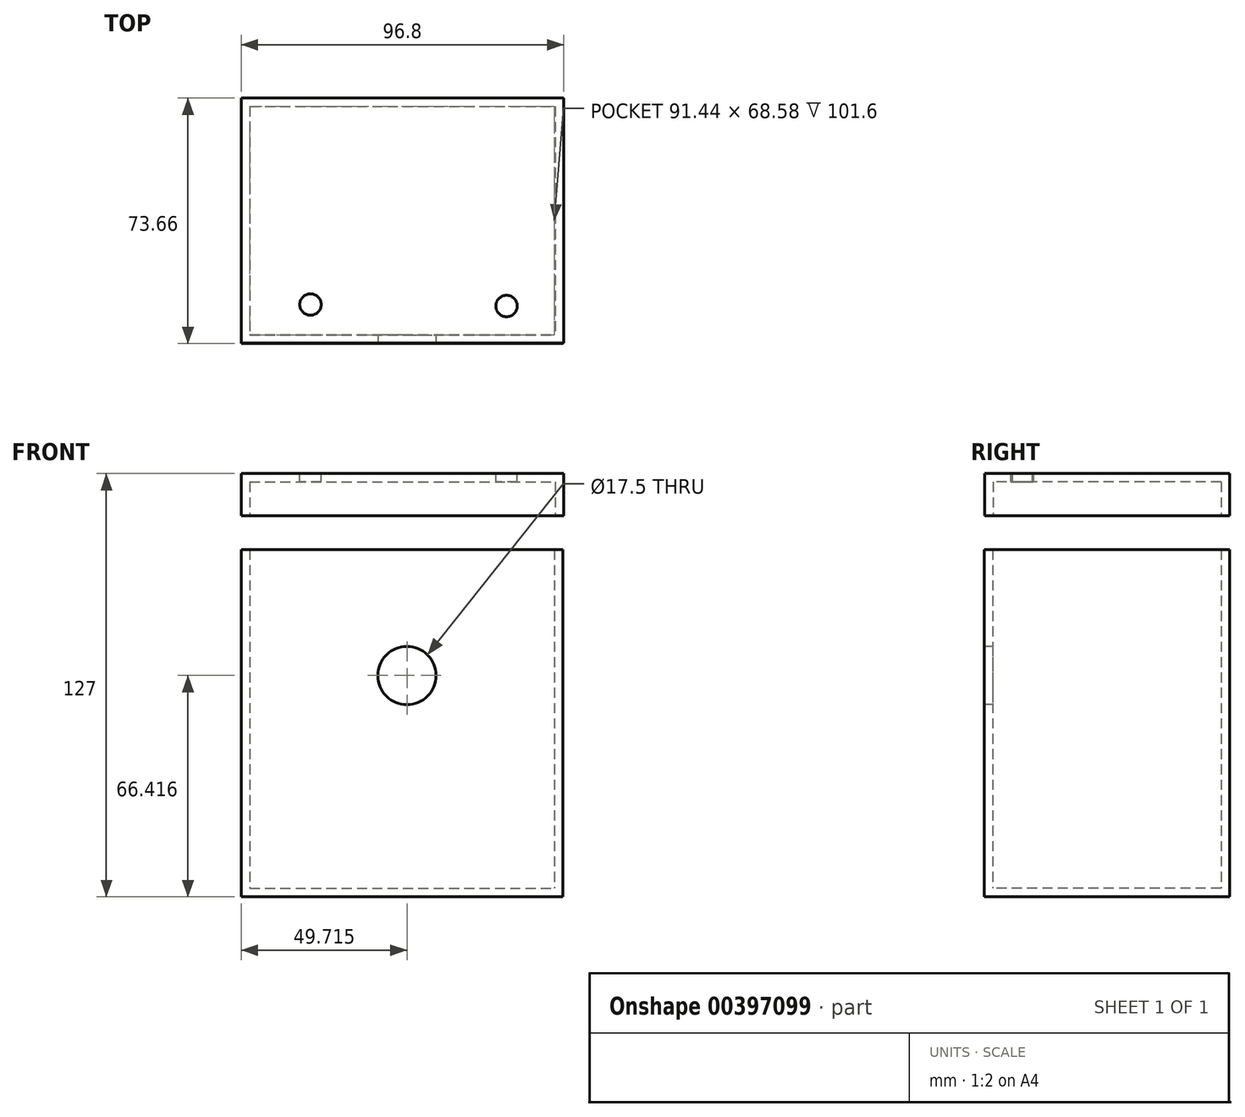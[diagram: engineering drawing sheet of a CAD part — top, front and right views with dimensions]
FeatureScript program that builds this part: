
annotation { "Feature Type Name" : "Feature", "Feature Type Description" : "" }
export const myFeature = defineFeature(function(context is Context, id is Id, definition is map)
    precondition{}
    {
        {
            var Q0;
            Q0=qCreatedBy(makeId("Top.planeOp"),FACE);
            var sketch = newSketch(context, id + "F0", { "sketchPlane" : qUnion([Q0])});
            skLineSegment(sketch, "E0.bottom", {"start": v(0, 0) * mm, "end": v(96.52, 0) * mm});
            skLineSegment(sketch, "E0.top", {"start": v(0, -73.66) * mm, "end": v(96.52, -73.66) * mm});
            skLineSegment(sketch, "E0.left", {"start": v(0, 0) * mm, "end": v(0, -73.66) * mm});
            skLineSegment(sketch, "E0.right", {"start": v(96.52, 0) * mm, "end": v(96.52, -73.66) * mm});
            skSolve(sketch);
        }
        {
            var Q0;
            Q0=makeQuery(id+"F0.imprint","IMPRINT",FACE,{"disambiguationData":[TD([[makeQuery(id+"F0.imprint","IMPRINT",EDGE,{"derivedFrom":sQuery(id+"F0.wireOp",EDGE,"E0.bottom")}),-1.0]])]});
            extrude(context, id + "F1", {"entities" : qUnion([Q0]), "depth" : 104.14 * mm});
        }
        {
            var Q0;
            Q0=makeQuery(id+"F1.opExtrude","CAP_FACE",FACE,{"disambiguationData":[OSD([sQuery(id+"F0.wireOp",EDGE,"E0.bottom"),sQuery(id+"F0.wireOp",EDGE,"E0.top"),sQuery(id+"F0.wireOp",EDGE,"E0.left"),sQuery(id+"F0.wireOp",EDGE,"E0.right")])],"isStart":false});
            shell(context, id + "F2", {"entities" : qUnion([Q0]), "thickness" : 2.54 * mm});
        }
        {
            var Q0;
            Q0=makeQuery(id+"F1.opExtrude","SWEPT_FACE",FACE,{"disambiguationData":[OSD([sQuery(id+"F0.wireOp",EDGE,"E0.top")])]});
            var sketch = newSketch(context, id + "F3", { "sketchPlane" : qUnion([Q0])});
            skCircle(sketch, "E1", {"center": v(49.71, 66.42) * mm, "radius": 8.75 * mm});
            skSolve(sketch);
        }
        {
            var Q0;
            Q0=makeQuery(id+"F3.imprint","IMPRINT",FACE,{"disambiguationData":[TD([[makeQuery(id+"F3.imprint","IMPRINT",EDGE,{"derivedFrom":sQuery(id+"F3.wireOp",EDGE,"E1")}),1.0]])]});
            extrude(context, id + "F4", {"entities" : qUnion([Q0]), "operationType" : NewBodyOperationType.REMOVE, "oppositeDirection" : true, "depth" : 25.4 * mm});
        }
        {
            var Q0;
            Q0=qCreatedBy(makeId("Top.planeOp"),FACE);
            cPlane(context, id + "F5", {"entities" : qUnion([Q0]), "cplaneType" : CPlaneType.OFFSET, "offset" : 114.3 * mm, "width" : 152.4 * mm, "height" : 152.4 * mm});
        }
        {
            var Q0;
            Q0=qCreatedBy(id+"F5.planeOp",FACE);
            var sketch = newSketch(context, id + "F6", { "sketchPlane" : qUnion([Q0])});
            skLineSegment(sketch, "E2.bottom", {"start": v(0, -73.52) * mm, "end": v(96.8, -73.52) * mm});
            skLineSegment(sketch, "E2.top", {"start": v(0, 0) * mm, "end": v(96.8, 0) * mm});
            skLineSegment(sketch, "E2.left", {"start": v(96.8, 0) * mm, "end": v(96.8, -73.52) * mm});
            skLineSegment(sketch, "E2.right", {"start": v(0, 0) * mm, "end": v(0, -73.52) * mm});
            skSolve(sketch);
        }
        {
            var Q0;
            Q0 = qSketchRegion(id + "F6", true);
            extrude(context, id + "F7", {"entities" : qUnion([Q0]), "depth" : 12.7 * mm});
        }
        {
            var Q0;
            Q0=makeQuery(id+"F7.opExtrude","CAP_FACE",FACE,{"disambiguationData":[OSD([sQuery(id+"F6.wireOp",EDGE,"E2.bottom"),sQuery(id+"F6.wireOp",EDGE,"E2.top"),sQuery(id+"F6.wireOp",EDGE,"E2.left"),sQuery(id+"F6.wireOp",EDGE,"E2.right")])],"isStart":true});
            shell(context, id + "F8", {"entities" : qUnion([Q0]), "thickness" : 2.54 * mm});
        }
        {
            var Q0;
            Q0=makeQuery(id+"F7.opExtrude","CAP_FACE",FACE,{"disambiguationData":[OSD([sQuery(id+"F6.wireOp",EDGE,"E2.bottom"),sQuery(id+"F6.wireOp",EDGE,"E2.top"),sQuery(id+"F6.wireOp",EDGE,"E2.left"),sQuery(id+"F6.wireOp",EDGE,"E2.right")])],"isStart":false});
            var sketch = newSketch(context, id + "F9", { "sketchPlane" : qUnion([Q0])});
            skCircle(sketch, "E3", {"center": v(20.77, -61.94) * mm, "radius": 3.21 * mm});
            skCircle(sketch, "E4", {"center": v(79.6, -62.39) * mm, "radius": 3.21 * mm});
            skSolve(sketch);
        }
        {
            var Q0;
            Q0=makeQuery(id+"F9.imprint","IMPRINT",FACE,{"disambiguationData":[TD([[makeQuery(id+"F9.imprint","IMPRINT",EDGE,{"derivedFrom":sQuery(id+"F9.wireOp",EDGE,"E3")}),1.0]])]});
            var Q1;
            Q1=makeQuery(id+"F9.imprint","IMPRINT",FACE,{"disambiguationData":[TD([[makeQuery(id+"F9.imprint","IMPRINT",EDGE,{"derivedFrom":sQuery(id+"F9.wireOp",EDGE,"E4")}),1.0]])]});
            extrude(context, id + "F10", {"entities" : qUnion([Q0, Q1]), "operationType" : NewBodyOperationType.REMOVE, "oppositeDirection" : true, "depth" : 2.54 * mm});
        }
    });
